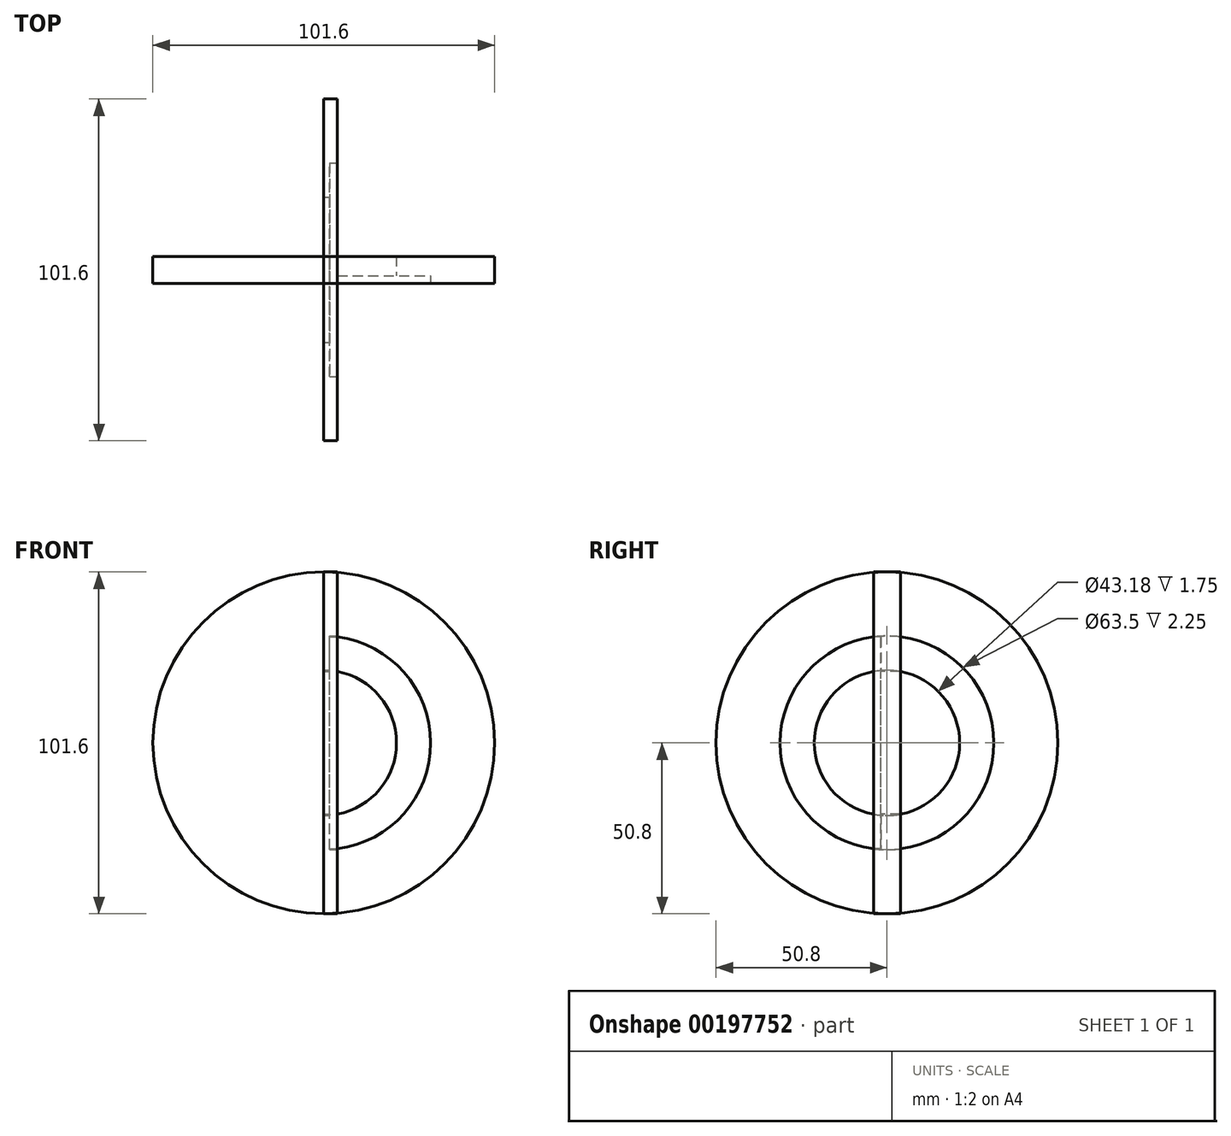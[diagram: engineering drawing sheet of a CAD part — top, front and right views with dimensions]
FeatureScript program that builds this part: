
annotation { "Feature Type Name" : "Feature", "Feature Type Description" : "" }
export const myFeature = defineFeature(function(context is Context, id is Id, definition is map)
    precondition{}
    {
        {
            assignVariable(context, id + "F0", {"name" : "LengthOutside", "anyValue" : 8});
        }
        {
            assignVariable(context, id + "F1", {"name" : "Depth", "anyValue" : 2.25});
        }
        {
            var Q0;
            Q0=qCreatedBy(makeId("Front.planeOp"),FACE);
            var sketch = newSketch(context, id + "F2", { "sketchPlane" : qUnion([Q0])});
            skCircle(sketch, "E0", {"center": v(0, 0) * mm, "radius": 21.59 * mm});
            skCircle(sketch, "E1", {"center": v(0, 0) * mm, "radius": 31.75 * mm});
            skCircle(sketch, "E2", {"center": v(0, 0) * mm, "radius": 50.8 * mm});
            skSolve(sketch);
        }
        {
            var Q0;
            Q0=makeQuery(id+"F2.imprint","IMPRINT",FACE,{"disambiguationData":[TD([[makeQuery(id+"F2.imprint","IMPRINT",EDGE,{"derivedFrom":sQuery(id+"F2.wireOp",EDGE,"E1")}),-1.0]])]});
            var Q1;
            Q1=makeQuery(id+"F2.imprint","IMPRINT",FACE,{"disambiguationData":[TD([[makeQuery(id+"F2.imprint","IMPRINT",EDGE,{"derivedFrom":sQuery(id+"F2.wireOp",EDGE,"E0")}),-1.0]])]});
            var Q2;
            Q2=makeQuery(id+"F2.imprint","IMPRINT",FACE,{"disambiguationData":[TD([[makeQuery(id+"F2.imprint","IMPRINT",EDGE,{"derivedFrom":sQuery(id+"F2.wireOp",EDGE,"E0")}),1.0]])]});
            extrude(context, id + "F3", {"entities" : qUnion([Q0, Q1, Q2]), "depth" : (getVariable(context, 'LengthOutside')) * mm, "symmetric" : true});
        }
        {
            var Q0;
            Q0=qCreatedBy(makeId("Right.planeOp"),FACE);
            var sketch = newSketch(context, id + "F4", { "sketchPlane" : qUnion([Q0])});
            skCircle(sketch, "E3", {"center": v(0, 0) * mm, "radius": 21.59 * mm});
            skCircle(sketch, "E4", {"center": v(0, 0) * mm, "radius": 31.75 * mm});
            skCircle(sketch, "E5", {"center": v(0, 0) * mm, "radius": 50.8 * mm});
            skSolve(sketch);
        }
        {
            var Q0;
            Q0=makeQuery(id+"F4.imprint","IMPRINT",FACE,{"disambiguationData":[TD([[makeQuery(id+"F4.imprint","IMPRINT",EDGE,{"derivedFrom":sQuery(id+"F4.wireOp",EDGE,"E4")}),-1.0]])]});
            var Q1;
            Q1=makeQuery(id+"F4.imprint","IMPRINT",FACE,{"disambiguationData":[TD([[makeQuery(id+"F4.imprint","IMPRINT",EDGE,{"derivedFrom":sQuery(id+"F4.wireOp",EDGE,"E3")}),-1.0]])]});
            var Q2;
            Q2=makeQuery(id+"F4.imprint","IMPRINT",FACE,{"disambiguationData":[TD([[makeQuery(id+"F4.imprint","IMPRINT",EDGE,{"derivedFrom":sQuery(id+"F4.wireOp",EDGE,"E3")}),1.0]])]});
            extrude(context, id + "F5", {"entities" : qUnion([Q0, Q1, Q2]), "depth" : (getVariable(context, 'LengthOutside') / 2) * mm});
        }
        {
            var Q0;
            Q0=makeQuery(id+"F5.opExtrude","CAP_FACE",FACE,{"disambiguationData":[OSD([sQuery(id+"F4.wireOp",EDGE,"E5")])],"isStart":false});
            var sketch = newSketch(context, id + "F6", { "sketchPlane" : qUnion([Q0])});
            skCircle(sketch, "E6", {"center": v(0, 0) * mm, "radius": 21.59 * mm});
            skCircle(sketch, "E7", {"center": v(0, 0) * mm, "radius": 31.75 * mm});
            skCircle(sketch, "E8", {"center": v(0, 0) * mm, "radius": 50.8 * mm});
            skSolve(sketch);
        }
        {
            var Q0;
            Q0=makeQuery(id+"F6.imprint","IMPRINT",FACE,{"disambiguationData":[TD([[makeQuery(id+"F6.imprint","IMPRINT",EDGE,{"derivedFrom":sQuery(id+"F6.wireOp",EDGE,"E6")}),1.0]])]});
            extrude(context, id + "F7", {"entities" : qUnion([Q0]), "operationType" : NewBodyOperationType.REMOVE, "oppositeDirection" : true, "depth" : (getVariable(context, 'LengthOutside') / 2) * mm});
        }
        {
            var Q0;
            Q0=makeQuery(id+"F6.imprint","IMPRINT",FACE,{"disambiguationData":[TD([[makeQuery(id+"F6.imprint","IMPRINT",EDGE,{"derivedFrom":sQuery(id+"F6.wireOp",EDGE,"E6")}),-1.0]])]});
            extrude(context, id + "F8", {"entities" : qUnion([Q0]), "operationType" : NewBodyOperationType.REMOVE, "oppositeDirection" : true, "depth" : (getVariable(context, 'Depth')) * mm});
        }
        {
            var Q0;
            Q0=makeQuery(id+"F3.opExtrude","CAP_FACE",FACE,{"disambiguationData":[OSD([sQuery(id+"F2.wireOp",EDGE,"E2")])],"isStart":false});
            var sketch = newSketch(context, id + "F9", { "sketchPlane" : qUnion([Q0])});
            skCircle(sketch, "E9", {"center": v(0, 0) * mm, "radius": 21.59 * mm});
            skCircle(sketch, "E10", {"center": v(0, 0) * mm, "radius": 31.75 * mm});
            skCircle(sketch, "E11", {"center": v(0, 0) * mm, "radius": 50.8 * mm});
            skSolve(sketch);
        }
        {
            var Q0;
            Q0=makeQuery(id+"F9.imprint","IMPRINT",FACE,{"disambiguationData":[TD([[makeQuery(id+"F9.imprint","IMPRINT",EDGE,{"derivedFrom":sQuery(id+"F9.wireOp",EDGE,"E9")}),1.0]])]});
            extrude(context, id + "F10", {"entities" : qUnion([Q0]), "operationType" : NewBodyOperationType.REMOVE, "oppositeDirection" : true, "depth" : (getVariable(context, 'LengthOutside')) * mm});
        }
        {
            var Q0;
            Q0=makeQuery(id+"F9.imprint","IMPRINT",FACE,{"disambiguationData":[TD([[makeQuery(id+"F9.imprint","IMPRINT",EDGE,{"derivedFrom":sQuery(id+"F9.wireOp",EDGE,"E9")}),-1.0]])]});
            extrude(context, id + "F11", {"entities" : qUnion([Q0]), "operationType" : NewBodyOperationType.REMOVE, "oppositeDirection" : true, "depth" : (getVariable(context, 'Depth')) * mm});
        }
        {
            var Q0;
            Q0=makeQuery(id+"F3.opExtrude","CAP_FACE",FACE,{"disambiguationData":[OSD([sQuery(id+"F2.wireOp",EDGE,"E2")])],"isStart":true});
            var sketch = newSketch(context, id + "F12", { "sketchPlane" : qUnion([Q0])});
            skCircle(sketch, "E12", {"center": v(0, 0) * mm, "radius": 21.59 * mm});
            skCircle(sketch, "E13", {"center": v(0, 0) * mm, "radius": 31.75 * mm});
            skCircle(sketch, "E14", {"center": v(0, 0) * mm, "radius": 50.8 * mm});
            skSolve(sketch);
        }
        {
            var Q0;
            Q0=makeQuery(id+"F12.imprint","IMPRINT",FACE,{"disambiguationData":[TD([[makeQuery(id+"F12.imprint","IMPRINT",EDGE,{"derivedFrom":sQuery(id+"F12.wireOp",EDGE,"E12")}),1.0]])]});
            extrude(context, id + "F13", {"entities" : qUnion([Q0]), "operationType" : NewBodyOperationType.REMOVE, "oppositeDirection" : true, "depth" : (getVariable(context, 'Depth')) * mm});
        }
    });
